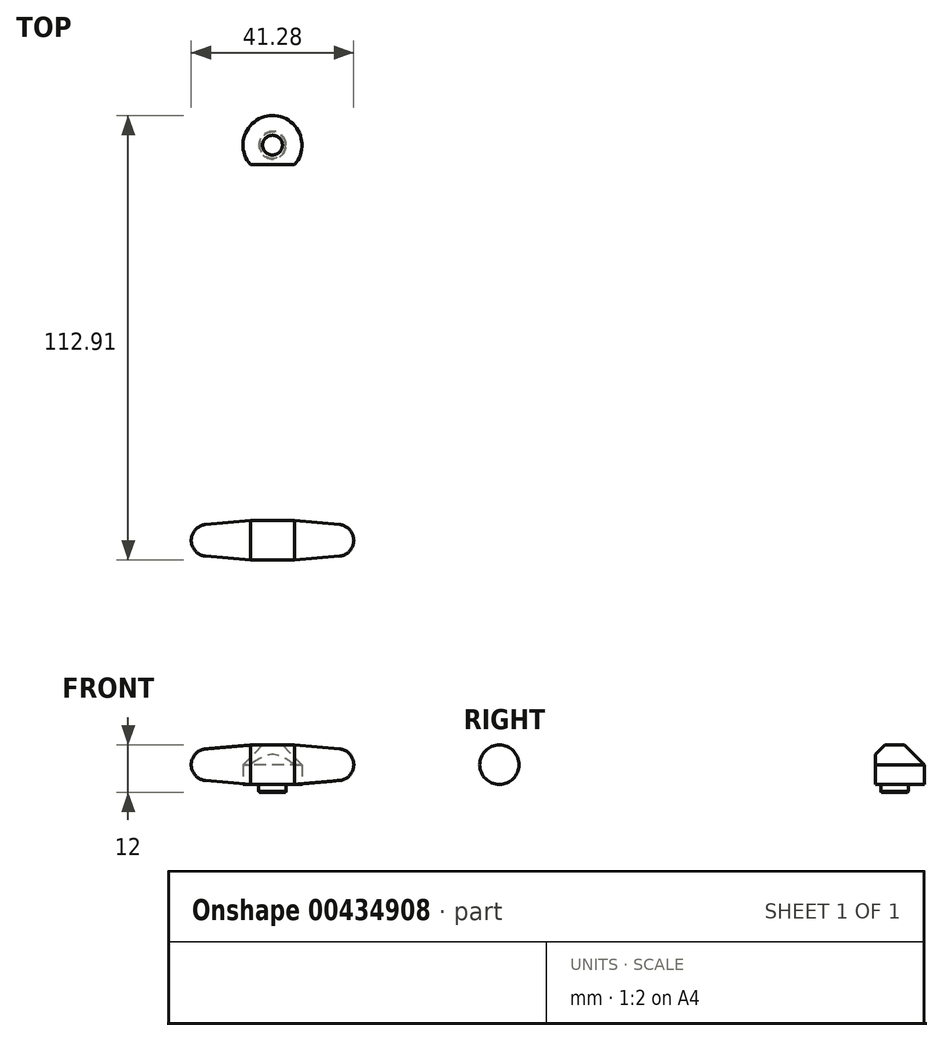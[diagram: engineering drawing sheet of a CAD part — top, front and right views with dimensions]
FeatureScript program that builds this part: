
annotation { "Feature Type Name" : "Feature", "Feature Type Description" : "" }
export const myFeature = defineFeature(function(context is Context, id is Id, definition is map)
    precondition{}
    {
        {
            var Q0;
            Q0=qCreatedBy(makeId("Top.planeOp"),FACE);
            var sketch = newSketch(context, id + "F0", { "sketchPlane" : qUnion([Q0])});
            skArc(sketch, "E0", {"start": v(5.64, -4.94) * mm, "mid": v(0, 7.5) * mm, "end": v(-5.64, -4.94) * mm});
            skLineSegment(sketch, "E1", {"start": v(5.64, -4.94) * mm, "end": v(5.64, -74.95) * mm});
            skLineSegment(sketch, "E2", {"start": v(-5.64, -4.94) * mm, "end": v(-5.64, -74.95) * mm});
            skLineSegment(sketch, "E3", {"start": v(5.64, -4.94) * mm, "end": v(5.64, -105.4) * mm});
            skLineSegment(sketch, "E4", {"start": v(5.64, -105.4) * mm, "end": v(-5.64, -105.4) * mm});
            skPoint(sketch, "E4.endSnap0", {"position": v(-5.64, -39.95) * mm});
            skLineSegment(sketch, "E5", {"start": v(-5.64, -105.4) * mm, "end": v(-5.64, -74.95) * mm});
            skSolve(sketch);
        }
        {
            var Q0;
            Q0=makeQuery(id+"F0.imprint","IMPRINT",FACE,{"disambiguationData":[TD([[makeQuery(id+"F0.imprint","IMPRINT",EDGE,{"derivedFrom":sQuery(id+"F0.wireOp",EDGE,"E0")}),1.0]])]});
            extrude(context, id + "F1", {"entities" : qUnion([Q0]), "depth" : 10 * mm});
        }
        {
            var Q0;
            Q0=makeQuery(id+"F1.opExtrude","CAP_FACE",FACE,{"disambiguationData":[OSD([sQuery(id+"F0.wireOp",EDGE,"E0"),sQuery(id+"F0.wireOp",EDGE,"fcuntJ9v-Vt85-QXs2-NARd-vfcrpFY0GrOK"),sQuery(id+"F0.wireOp",EDGE,"E1"),sQuery(id+"F0.wireOp",EDGE,"E2")])],"isStart":true});
            var sketch = newSketch(context, id + "F2", { "sketchPlane" : qUnion([Q0])});
            skCircle(sketch, "E6", {"center": v(0, 0) * mm, "radius": 3.5 * mm});
            skSolve(sketch);
        }
        {
            var Q0;
            Q0=makeQuery(id+"F2.imprint","IMPRINT",FACE,{"disambiguationData":[TD([[makeQuery(id+"F2.imprint","IMPRINT",EDGE,{"derivedFrom":sQuery(id+"F2.wireOp",EDGE,"E6")}),1.0]])]});
            extrude(context, id + "F3", {"entities" : qUnion([Q0]), "operationType" : NewBodyOperationType.ADD, "depth" : 2 * mm});
        }
        {
            var Q0;
            Q0=makeQuery(id+"F3.opExtrude","CAP_EDGE",EDGE,{"disambiguationData":[OSD([sQuery(id+"F2.wireOp",EDGE,"E6")])],"isStart":false});
            chamfer(context, id + "F4", {"entities" : qUnion([Q0]), "width" : .2 * mm, "tangentPropagation" : true});
        }
        {
            var Q0;
            Q0=makeQuery(id+"F1.opExtrude","SWEPT_FACE",FACE,{"disambiguationData":[OSD([sQuery(id+"F0.wireOp",EDGE,"E3")])]});
            var sketch = newSketch(context, id + "F5", { "sketchPlane" : qUnion([Q0])});
            skLineSegment(sketch, "E7", {"start": v(-105.4, 5) * mm, "end": v(-100.4, 5) * mm, "construction": true});
            skCircle(sketch, "E8", {"center": v(-100.4, 5) * mm, "radius": 5 * mm});
            skSolve(sketch);
        }
        {
            var Q0;
            {var subQ0=sQuery(id+"F5.wireOp",EDGE,"E8");var subQ1=sQuery(id+"F0.wireOp",EDGE,"E3");var subQ3=makeQuery(id+"F5.imprint","INTERSECT",VERTEX,{"derivedFrom":[makeQuery(id+"F1.opExtrude","CAP_EDGE",EDGE,{"disambiguationData":[OSD([subQ1])],"isStart":false}),subQ0]});Q0=makeQuery(id+"F5.imprint","IMPRINT",FACE,{"disambiguationData":[TD([[makeQuery(id+"F5.imprint","IMPRINT",EDGE,{"disambiguationData":[TD([[subQ3,1.0]])],"derivedFrom":subQ0}),1.0]])]});}
            extrude(context, id + "F6", {"entities" : qUnion([Q0]), "operationType" : NewBodyOperationType.ADD, "depth" : 15 * mm, "hasDraft" : true, "draftAngle" : 5 * degree, "draftPullDirection" : true});
        }
        {
            var Q0;
            Q0=makeQuery(id+"F1.opExtrude","SWEPT_FACE",FACE,{"disambiguationData":[OSD([sQuery(id+"F0.wireOp",EDGE,"E2"),sQuery(id+"F0.wireOp",EDGE,"E5")])]});
            var sketch = newSketch(context, id + "F7", { "sketchPlane" : qUnion([Q0])});
            skLineSegment(sketch, "E9", {"start": v(105.4, 5) * mm, "end": v(100.4, 5) * mm, "construction": true});
            skCircle(sketch, "E10", {"center": v(100.4, 5) * mm, "radius": 5 * mm});
            skSolve(sketch);
        }
        {
            var Q0;
            {var subQ0=sQuery(id+"F7.wireOp",EDGE,"E10");var subQ1=sQuery(id+"F0.wireOp",EDGE,"E5");var subQ2=sQuery(id+"F0.wireOp",EDGE,"E2");var subQ3=makeQuery(id+"F7.imprint","INTERSECT",VERTEX,{"derivedFrom":[makeQuery(id+"F1.opExtrude","CAP_EDGE",EDGE,{"disambiguationData":[OSD([subQ2,subQ1])],"isStart":false}),subQ0]});Q0=makeQuery(id+"F7.imprint","IMPRINT",FACE,{"disambiguationData":[TD([[makeQuery(id+"F7.imprint","IMPRINT",EDGE,{"disambiguationData":[TD([[subQ3,1.0]])],"derivedFrom":subQ0}),1.0]])]});}
            extrude(context, id + "F8", {"entities" : qUnion([Q0]), "operationType" : NewBodyOperationType.ADD, "depth" : 15 * mm, "hasDraft" : true, "draftAngle" : 5 * degree, "draftPullDirection" : true});
        }
        {
            var Q0;
            {var subQ0=sQuery(id+"F0.wireOp",EDGE,"E5");var subQ1=sQuery(id+"F0.wireOp",EDGE,"E4");var subQ2=sQuery(id+"F0.wireOp",EDGE,"E2");var subQ3=makeQuery(id+"F1.opExtrude","SWEPT_FACE",FACE,{"disambiguationData":[OSD([subQ2,subQ0])]});Q0=makeQuery(id+"F8.boolean.opBoolean","SPLIT",FACE,{"disambiguationData":[TD([makeQuery(id+"F1.opExtrude","CAP_FACE",FACE,{"disambiguationData":[OSD([sQuery(id+"F0.wireOp",EDGE,"E0"),subQ2,sQuery(id+"F0.wireOp",EDGE,"E3"),subQ1,subQ0])],"isStart":false}),subQ3,makeQuery(id+"F1.opExtrude","SWEPT_FACE",FACE,{"disambiguationData":[OSD([subQ1])]}),makeQuery(id+"F8.opExtrude","SWEPT_FACE",FACE,{"disambiguationData":[OSD([sQuery(id+"F7.wireOp",EDGE,"E10")])]})])],"derivedFrom":subQ3});}
            var Q1;
            {var subQ0=sQuery(id+"F0.wireOp",EDGE,"E5");var subQ1=sQuery(id+"F0.wireOp",EDGE,"E4");var subQ2=sQuery(id+"F0.wireOp",EDGE,"E2");var subQ3=makeQuery(id+"F1.opExtrude","SWEPT_FACE",FACE,{"disambiguationData":[OSD([subQ2,subQ0])]});Q1=makeQuery(id+"F8.boolean.opBoolean","SPLIT",FACE,{"disambiguationData":[TD([makeQuery(id+"F1.opExtrude","CAP_FACE",FACE,{"disambiguationData":[OSD([sQuery(id+"F0.wireOp",EDGE,"E0"),subQ2,sQuery(id+"F0.wireOp",EDGE,"E3"),subQ1,subQ0])],"isStart":true}),subQ3,makeQuery(id+"F1.opExtrude","SWEPT_FACE",FACE,{"disambiguationData":[OSD([subQ1])]}),makeQuery(id+"F8.opExtrude","SWEPT_FACE",FACE,{"disambiguationData":[OSD([sQuery(id+"F7.wireOp",EDGE,"E10")])]})])],"derivedFrom":subQ3});}
            extrude(context, id + "F9", {"entities" : qUnion([Q0, Q1]), "operationType" : NewBodyOperationType.REMOVE, "oppositeDirection" : true, "depth" : 25 * mm});
        }
        {
            var Q0;
            {var subQ0=sQuery(id+"F0.wireOp",EDGE,"E0");var subQ1=sQuery(id+"F0.wireOp",EDGE,"E5");var subQ2=sQuery(id+"F0.wireOp",EDGE,"E2");Q0=makeQuery(id+"F8.boolean.opBoolean","SPLIT",EDGE,{"disambiguationData":[TD([makeQuery(id+"F1.opExtrude","SWEPT_FACE",FACE,{"disambiguationData":[OSD([subQ0])]})])],"derivedFrom":makeQuery(id+"F1.opExtrude","CAP_EDGE",EDGE,{"disambiguationData":[OSD([subQ2,subQ1])],"isStart":false})});}
            var Q1;
            {var subQ0=sQuery(id+"F0.wireOp",EDGE,"E0");var subQ1=sQuery(id+"F0.wireOp",EDGE,"E3");Q1=makeQuery(id+"F6.boolean.opBoolean","SPLIT",EDGE,{"disambiguationData":[TD([makeQuery(id+"F1.opExtrude","SWEPT_FACE",FACE,{"disambiguationData":[OSD([subQ0])]})])],"derivedFrom":makeQuery(id+"F1.opExtrude","CAP_EDGE",EDGE,{"disambiguationData":[OSD([subQ1])],"isStart":false})});}
            var Q2;
            {var subQ0=sQuery(id+"F0.wireOp",EDGE,"E0");var subQ1=sQuery(id+"F0.wireOp",EDGE,"E5");var subQ2=sQuery(id+"F0.wireOp",EDGE,"E2");Q2=makeQuery(id+"F8.boolean.opBoolean","SPLIT",EDGE,{"disambiguationData":[TD([makeQuery(id+"F1.opExtrude","SWEPT_FACE",FACE,{"disambiguationData":[OSD([subQ0])]})])],"derivedFrom":makeQuery(id+"F1.opExtrude","CAP_EDGE",EDGE,{"disambiguationData":[OSD([subQ2,subQ1])],"isStart":true})});}
            var Q3;
            {var subQ0=sQuery(id+"F0.wireOp",EDGE,"E0");var subQ1=sQuery(id+"F0.wireOp",EDGE,"E3");Q3=makeQuery(id+"F6.boolean.opBoolean","SPLIT",EDGE,{"disambiguationData":[TD([makeQuery(id+"F1.opExtrude","SWEPT_FACE",FACE,{"disambiguationData":[OSD([subQ0])]})])],"derivedFrom":makeQuery(id+"F1.opExtrude","CAP_EDGE",EDGE,{"disambiguationData":[OSD([subQ1])],"isStart":true})});}
            var Q4;
            Q4=makeQuery(id+"F1.opExtrude","CAP_EDGE",EDGE,{"disambiguationData":[OSD([sQuery(id+"F0.wireOp",EDGE,"E0")])],"isStart":false});
            chamfer(context, id + "F10", {"entities" : qUnion([Q0, Q1, Q2, Q3, Q4]), "width" : 5 * mm, "tangentPropagation" : true});
        }
        {
            var Q0;
            Q0=makeQuery(id+"F8.opExtrude","CAP_EDGE",EDGE,{"disambiguationData":[OSD([sQuery(id+"F7.wireOp",EDGE,"E10")])],"isStart":false});
            var Q1;
            Q1=makeQuery(id+"F6.opExtrude","CAP_EDGE",EDGE,{"disambiguationData":[OSD([sQuery(id+"F5.wireOp",EDGE,"E8")])],"isStart":false});
            fillet(context, id + "F11", {"entities" : qUnion([Q0, Q1]), "radius" : 4 * mm, "tangentPropagation" : true, "allowEdgeOverflow" : false});
        }
    });
